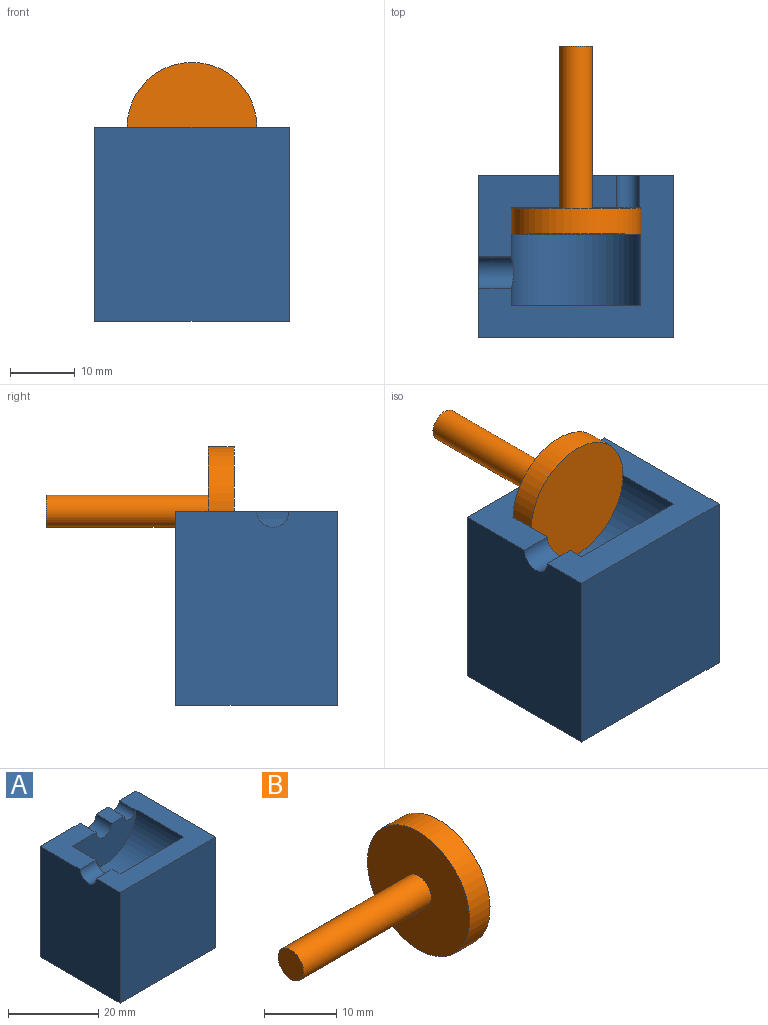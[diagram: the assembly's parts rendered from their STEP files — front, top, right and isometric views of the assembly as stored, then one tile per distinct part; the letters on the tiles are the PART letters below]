
ASSEMBLY  parts=2 mates=1
PART A: 14 faces, bbox 30x25x30 mm
  f0: plane 12.5x12.5mm, normal (0,0,1), area 100mm2, adj f4,f5,f7,f8,f12,f13
  f1: plane 30x25mm, normal (0,0,1), area 263.7mm2, adj f3,f4,f5,f7,f8,f9,f10,f11
  f2: plane 5x3.75mm, normal (0,0,1), area 18.8mm2, adj f7,f8,f11,f12
  f3: plane 30x25mm, normal (1,0,0), area 750mm2, adj f1,f6,f8,f10
  f4: cylinder r=10mm len=20mm, axis (0,1,0), area 461.4mm2, adj f0,f1,f7,f9,f13
  f5: plane 30x25mm, normal (-1,0,0), area 740.2mm2, adj f0,f1,f6,f8,f10,f13
  f6: plane 30x25mm, normal (0,0,-1), area 750mm2, adj f3,f5,f8,f10
  f7: plane 20x10mm, normal (0,-1,0), area 142.5mm2, adj f0,f1,f2,f4,f11,f12
  f8: plane 30x30mm, normal (0,1,0), area 885.4mm2, adj f0,f1,f2,f3,f5,f6,f11,f12
  f9: plane 20x10mm, normal (0,1,0), area 157.1mm2, adj f1,f4
  f10: plane 30x30mm, normal (0,-1,0), area 900mm2, adj f1,f3,f5,f6
  f11: cylinder r=1.75mm len=5mm, axis (0,1,0), area 27.5mm2, adj f1,f2,f7,f8
  f12: cylinder r=2.5mm len=5mm, axis (0,1,0), area 39.3mm2, adj f0,f2,f7,f8
  f13: cylinder r=2.5mm len=5.32mm, axis (1,0,0), area 40.5mm2, adj f0,f1,f4,f5
PART B: 5 faces, bbox 29x20x20 mm
  f0: cylinder r=10mm len=20mm, axis (-1,0,0), area 251.3mm2, adj f1,f2
  f1: plane 20x20mm, normal (1,0,0), area 314.2mm2, adj f0
  f2: plane 20x20mm, normal (-1,0,0), area 294.5mm2, adj f0,f3
  f3: cylinder r=2.5mm len=25mm, axis (1,0,0), area 392.7mm2, adj f2,f4
  f4: plane 5x5mm, normal (-1,0,0), area 19.6mm2, adj f3
PLACE A t=(2.02,16.52,1.49)mm fixed
PLACE B rot(axis=(0,0,-1),90deg) t=(2.02,6.48,16.49)mm
MATE slider B.f0 <-> A.f4  axis (0,-1,0) through (2.02,2.48,16.49)mm
